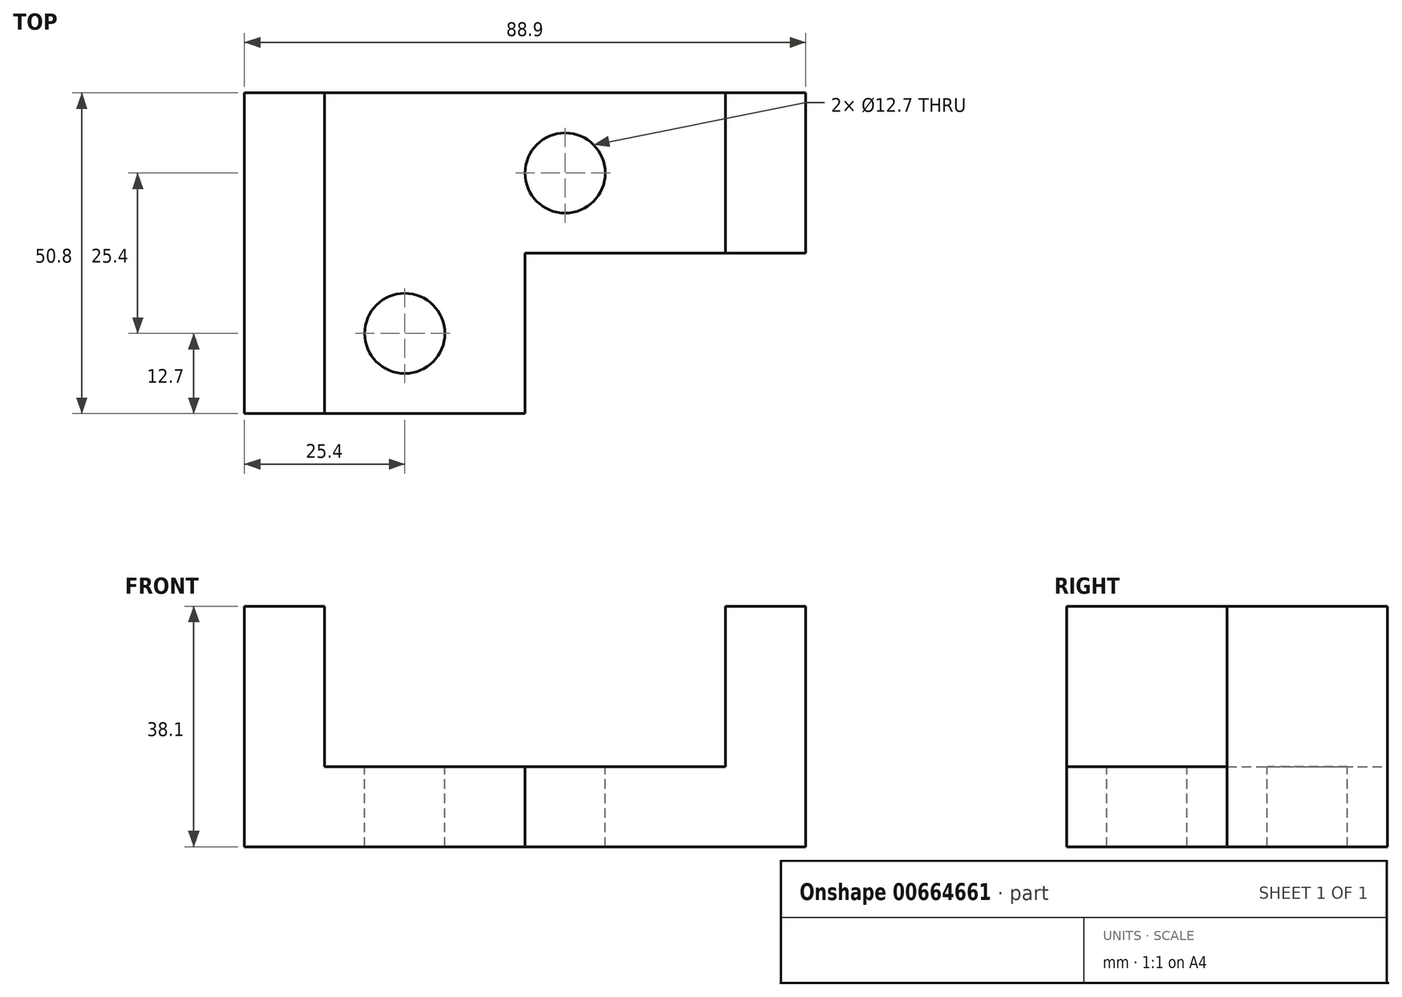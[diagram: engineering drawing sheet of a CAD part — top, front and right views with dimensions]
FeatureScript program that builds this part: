
annotation { "Feature Type Name" : "Feature", "Feature Type Description" : "" }
export const myFeature = defineFeature(function(context is Context, id is Id, definition is map)
    precondition{}
    {
        {
            var Q0;
            Q0=qCreatedBy(makeId("Front.planeOp"),FACE);
            var sketch = newSketch(context, id + "F0", { "sketchPlane" : qUnion([Q0])});
            skLineSegment(sketch, "E0.bottom", {"start": v(-44.45, 19.05) * mm, "end": v(44.45, 19.05) * mm});
            skLineSegment(sketch, "E0.top", {"start": v(-44.45, -19.05) * mm, "end": v(44.45, -19.05) * mm});
            skLineSegment(sketch, "E0.left", {"start": v(-44.45, 19.05) * mm, "end": v(-44.45, -19.05) * mm});
            skLineSegment(sketch, "E0.right", {"start": v(44.45, 19.05) * mm, "end": v(44.45, -19.05) * mm});
            skPoint(sketch, "E0.middle", {"position": v(0, 0) * mm});
            skSolve(sketch);
        }
        {
            var Q0;
            Q0=makeQuery(id+"F0.imprint","IMPRINT",FACE,{"disambiguationData":[TD([[makeQuery(id+"F0.imprint","IMPRINT",EDGE,{"derivedFrom":sQuery(id+"F0.wireOp",EDGE,"E0.bottom")}),-1.0]])]});
            var sketch = newSketch(context, id + "F1", { "sketchPlane" : qUnion([Q0])});
            skLineSegment(sketch, "E1.bottom", {"start": v(-31.75, 19.05) * mm, "end": v(31.75, 19.05) * mm});
            skLineSegment(sketch, "E1.top", {"start": v(-31.75, -6.35) * mm, "end": v(31.75, -6.35) * mm});
            skLineSegment(sketch, "E1.left", {"start": v(-31.75, 19.05) * mm, "end": v(-31.75, -6.35) * mm});
            skLineSegment(sketch, "E1.right", {"start": v(31.75, 19.05) * mm, "end": v(31.75, -6.35) * mm});
            skSolve(sketch);
        }
        {
            var Q0;
            Q0=makeQuery(id+"F0.imprint","IMPRINT",FACE,{"disambiguationData":[TD([[makeQuery(id+"F0.imprint","IMPRINT",EDGE,{"derivedFrom":sQuery(id+"F0.wireOp",EDGE,"E0.bottom")}),-1.0]])]});
            extrude(context, id + "F2", {"entities" : qUnion([Q0]), "depth" : 50.8 * mm, "offsetDistance" : 25.4 * mm});
        }
        {
            var Q0;
            Q0=makeQuery(id+"F1.imprint","IMPRINT",FACE,{"disambiguationData":[TD([[makeQuery(id+"F1.imprint","IMPRINT",EDGE,{"derivedFrom":sQuery(id+"F1.wireOp",EDGE,"E1.bottom")}),-1.0]])]});
            extrude(context, id + "F3", {"entities" : qUnion([Q0]), "operationType" : NewBodyOperationType.REMOVE, "endBound" : BoundingType.THROUGH_ALL, "depth" : 25.4 * mm, "offsetDistance" : 25.4 * mm});
        }
        {
            var Q0;
            {var subQ0=sQuery(id+"F0.wireOp",EDGE,"E0.right");var subQ3=sQuery(id+"F0.wireOp",EDGE,"E0.bottom");Q0=makeQuery(id+"F3.boolean.opBoolean","SPLIT",FACE,{"disambiguationData":[TD([makeQuery(id+"F2.opExtrude","SWEPT_FACE",FACE,{"disambiguationData":[OSD([subQ0])]})])],"derivedFrom":makeQuery(id+"F2.opExtrude","SWEPT_FACE",FACE,{"disambiguationData":[OSD([subQ3])]})});}
            var sketch = newSketch(context, id + "F4", { "sketchPlane" : qUnion([Q0])});
            skLineSegment(sketch, "E2.bottom", {"start": v(44.45, -50.8) * mm, "end": v(0, -50.8) * mm});
            skLineSegment(sketch, "E2.top", {"start": v(44.45, -25.4) * mm, "end": v(0, -25.4) * mm});
            skLineSegment(sketch, "E2.left", {"start": v(44.45, -50.8) * mm, "end": v(44.45, -25.4) * mm});
            skLineSegment(sketch, "E2.right", {"start": v(0, -50.8) * mm, "end": v(0, -25.4) * mm});
            skSolve(sketch);
        }
        {
            var Q0;
            {var subQ3=sQuery(id+"F4.wireOp",EDGE,"E2.right");Q0=makeQuery(id+"F4.imprint","IMPRINT",FACE,{"disambiguationData":[TD([[makeQuery(id+"F4.imprint","IMPRINT",EDGE,{"derivedFrom":subQ3}),-1.0]])]});}
            var Q1;
            {var subQ0=sQuery(id+"F4.wireOp",EDGE,"E2.left");Q1=makeQuery(id+"F4.imprint","IMPRINT",FACE,{"disambiguationData":[TD([[makeQuery(id+"F4.imprint","IMPRINT",EDGE,{"derivedFrom":subQ0}),1.0]])]});}
            extrude(context, id + "F5", {"entities" : qUnion([Q0, Q1]), "operationType" : NewBodyOperationType.REMOVE, "endBound" : BoundingType.THROUGH_ALL, "oppositeDirection" : true, "depth" : 25.4 * mm, "offsetDistance" : 25.4 * mm});
        }
        {
            var Q0;
            Q0=makeQuery(id+"F3.boolean.opBoolean","COPY",FACE,{"derivedFrom":makeQuery(id+"F3.opExtrude","SWEPT_FACE",FACE,{"disambiguationData":[OSD([sQuery(id+"F1.wireOp",EDGE,"E1.top")])]})});
            var sketch = newSketch(context, id + "F6", { "sketchPlane" : qUnion([Q0])});
            skCircle(sketch, "E3", {"center": v(6.35, -12.7) * mm, "radius": 6.35 * mm});
            skCircle(sketch, "E4", {"center": v(-19.05, -38.1) * mm, "radius": 6.35 * mm});
            skSolve(sketch);
        }
        {
            var Q0;
            Q0=makeQuery(id+"F6.imprint","IMPRINT",FACE,{"disambiguationData":[TD([[makeQuery(id+"F6.imprint","IMPRINT",EDGE,{"derivedFrom":sQuery(id+"F6.wireOp",EDGE,"E4")}),1.0]])]});
            var Q1;
            Q1=makeQuery(id+"F6.imprint","IMPRINT",FACE,{"disambiguationData":[TD([[makeQuery(id+"F6.imprint","IMPRINT",EDGE,{"derivedFrom":sQuery(id+"F6.wireOp",EDGE,"E3")}),1.0]])]});
            var Q2;
            Q2=sQuery(id+"F6.wireOp",EDGE,"E3");
            var Q3;
            Q3=sQuery(id+"F6.wireOp",EDGE,"E4");
            extrude(context, id + "F7", {"entities" : qUnion([Q0, Q1]), "operationType" : NewBodyOperationType.REMOVE, "surfaceEntities" : qUnion([Q2, Q3]), "endBound" : BoundingType.THROUGH_ALL, "oppositeDirection" : true, "depth" : 25.4 * mm, "offsetDistance" : 25.4 * mm});
        }
    });
